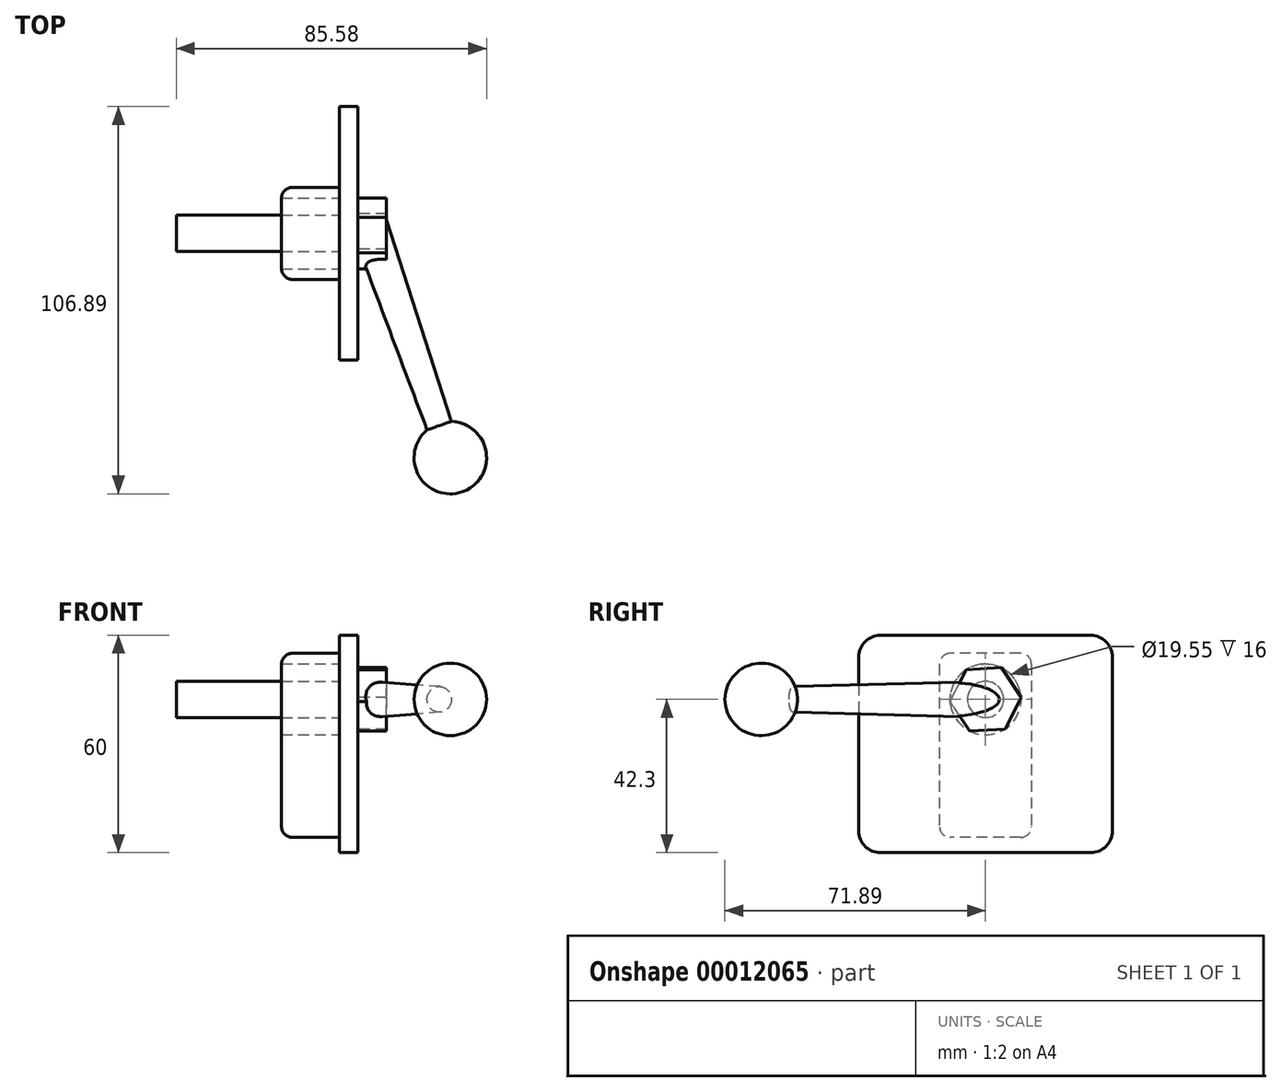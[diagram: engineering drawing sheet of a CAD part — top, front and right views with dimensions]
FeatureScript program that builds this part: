
annotation { "Feature Type Name" : "Feature", "Feature Type Description" : "" }
export const myFeature = defineFeature(function(context is Context, id is Id, definition is map)
    precondition{}
    {
        {
            var Q0;
            Q0=qCreatedBy(makeId("Right.planeOp"),FACE);
            var sketch = newSketch(context, id + "F0", { "sketchPlane" : qUnion([Q0])});
            skCircle(sketch, "E0.cCircle", {"center": v(0, 0) * mm, "radius": 8.5 * mm, "construction": true});
            skLineSegment(sketch, "E0.0", {"start": v(9.8, 0.59) * mm, "end": v(5.4, -8.2) * mm});
            skLineSegment(sketch, "E0.1", {"start": v(5.4, -8.2) * mm, "end": v(-4.39, -8.78) * mm});
            skLineSegment(sketch, "E0.2", {"start": v(-4.39, -8.78) * mm, "end": v(-9.8, -0.59) * mm});
            skLineSegment(sketch, "E0.3", {"start": v(-9.8, -0.59) * mm, "end": v(-5.4, 8.2) * mm});
            skLineSegment(sketch, "E0.4", {"start": v(-5.4, 8.2) * mm, "end": v(4.39, 8.78) * mm});
            skLineSegment(sketch, "E0.5", {"start": v(4.39, 8.78) * mm, "end": v(9.8, 0.59) * mm});
            skPoint(sketch, "E0.0.midPoint", {"position": v(7.6, -3.8) * mm});
            skSolve(sketch);
        }
        {
            var Q0;
            Q0 = qSketchRegion(id + "F0", true);
            extrude(context, id + "F1", {"entities" : qUnion([Q0]), "depth" : 8 * mm});
        }
        {
            var Q0;
            Q0=makeQuery(id+"F1.opExtrude","CAP_FACE",FACE,{"disambiguationData":[OSD([sQuery(id+"F0.wireOp",EDGE,"E0.0"),sQuery(id+"F0.wireOp",EDGE,"E0.1"),sQuery(id+"F0.wireOp",EDGE,"E0.2"),sQuery(id+"F0.wireOp",EDGE,"E0.3"),sQuery(id+"F0.wireOp",EDGE,"E0.4"),sQuery(id+"F0.wireOp",EDGE,"E0.5")])],"isStart":true});
            var sketch = newSketch(context, id + "F2", { "sketchPlane" : qUnion([Q0])});
            skCircle(sketch, "E1", {"center": v(0, 0) * mm, "radius": 5 * mm});
            skSolve(sketch);
        }
        {
            var Q0;
            Q0 = qSketchRegion(id + "F2", true);
            extrude(context, id + "F3", {"entities" : qUnion([Q0]), "operationType" : NewBodyOperationType.ADD, "depth" : 50 * mm});
        }
        {
            var Q0;
            Q0=qCreatedBy(makeId("Right.planeOp"),FACE);
            var sketch = newSketch(context, id + "F4", { "sketchPlane" : qUnion([Q0])});
            skLineSegment(sketch, "E2.bottom", {"start": v(29, 17.7) * mm, "end": v(-29, 17.7) * mm});
            skLineSegment(sketch, "E2.top", {"start": v(29, -42.3) * mm, "end": v(-29, -42.3) * mm});
            skLineSegment(sketch, "E2.left", {"start": v(35, 11.7) * mm, "end": v(35, -36.3) * mm});
            skLineSegment(sketch, "E2.right", {"start": v(-35, 11.7) * mm, "end": v(-35, -36.3) * mm});
            skPoint(sketch, "E3.visualSharp", {"position": v(35, 17.7) * mm});
            skArc(sketch, "E3.filletArc", {"start": v(35, 11.7) * mm, "mid": v(33.24, 15.94) * mm, "end": v(29, 17.7) * mm});
            skPoint(sketch, "E4.visualSharp", {"position": v(-35, 17.7) * mm});
            skArc(sketch, "E4.filletArc", {"start": v(-29, 17.7) * mm, "mid": v(-33.24, 15.94) * mm, "end": v(-35, 11.7) * mm});
            skPoint(sketch, "E5.visualSharp", {"position": v(-35, -42.3) * mm});
            skArc(sketch, "E5.filletArc", {"start": v(-35, -36.3) * mm, "mid": v(-33.24, -40.54) * mm, "end": v(-29, -42.3) * mm});
            skPoint(sketch, "E6.visualSharp", {"position": v(35, -42.3) * mm});
            skArc(sketch, "E6.filletArc", {"start": v(29, -42.3) * mm, "mid": v(33.24, -40.54) * mm, "end": v(35, -36.3) * mm});
            skSolve(sketch);
        }
        {
            var Q0;
            Q0 = qSketchRegion(id + "F4", true);
            extrude(context, id + "F5", {"entities" : qUnion([Q0]), "operationType" : NewBodyOperationType.ADD, "oppositeDirection" : true, "depth" : 5 * mm});
        }
        {
            var Q0;
            Q0=makeQuery(id+"F5.opExtrude","CAP_FACE",FACE,{"disambiguationData":[OSD([sQuery(id+"F4.wireOp",EDGE,"E2.bottom"),sQuery(id+"F4.wireOp",EDGE,"E2.top"),sQuery(id+"F4.wireOp",EDGE,"E2.left"),sQuery(id+"F4.wireOp",EDGE,"E2.right"),sQuery(id+"F4.wireOp",EDGE,"E3.filletArc"),sQuery(id+"F4.wireOp",EDGE,"E4.filletArc"),sQuery(id+"F4.wireOp",EDGE,"E5.filletArc"),sQuery(id+"F4.wireOp",EDGE,"E6.filletArc")])],"isStart":false});
            var sketch = newSketch(context, id + "F6", { "sketchPlane" : qUnion([Q0])});
            skLineSegment(sketch, "E7.bottom", {"start": v(-9.7, 12.7) * mm, "end": v(9.7, 12.7) * mm});
            skLineSegment(sketch, "E7.top", {"start": v(-9.7, -38.1) * mm, "end": v(9.7, -38.1) * mm});
            skLineSegment(sketch, "E7.left", {"start": v(-12.7, 9.7) * mm, "end": v(-12.7, -35.1) * mm});
            skLineSegment(sketch, "E7.right", {"start": v(12.7, 9.7) * mm, "end": v(12.7, -35.1) * mm});
            skCircle(sketch, "E8", {"center": v(0, 0) * mm, "radius": 9.78 * mm});
            skPoint(sketch, "E9.visualSharp", {"position": v(-12.7, 12.7) * mm});
            skArc(sketch, "E9.filletArc", {"start": v(-9.7, 12.7) * mm, "mid": v(-11.82, 11.82) * mm, "end": v(-12.7, 9.7) * mm});
            skPoint(sketch, "E10.visualSharp", {"position": v(12.7, 12.7) * mm});
            skArc(sketch, "E10.filletArc", {"start": v(12.7, 9.7) * mm, "mid": v(11.82, 11.82) * mm, "end": v(9.7, 12.7) * mm});
            skPoint(sketch, "E11.visualSharp", {"position": v(12.7, -38.1) * mm});
            skArc(sketch, "E11.filletArc", {"start": v(9.7, -38.1) * mm, "mid": v(11.82, -37.22) * mm, "end": v(12.7, -35.1) * mm});
            skPoint(sketch, "E12.visualSharp", {"position": v(-12.7, -38.1) * mm});
            skArc(sketch, "E12.filletArc", {"start": v(-12.7, -35.1) * mm, "mid": v(-11.82, -37.22) * mm, "end": v(-9.7, -38.1) * mm});
            skSolve(sketch);
        }
        {
            var Q0;
            Q0 = qSketchRegion(id + "F6", true);
            extrude(context, id + "F7", {"entities" : qUnion([Q0]), "operationType" : NewBodyOperationType.ADD, "depth" : 16 * mm});
        }
        {
            var Q0;
            Q0=makeQuery(id+"F7.opExtrude","CAP_EDGE",EDGE,{"disambiguationData":[OSD([sQuery(id+"F6.wireOp",EDGE,"E7.left")])],"isStart":false});
            fillet(context, id + "F8", {"entities" : qUnion([Q0]), "radius" : 3 * mm, "tangentPropagation" : true, "allowEdgeOverflow" : false});
        }
        {
            var Q0;
            Q0=qCreatedBy(makeId("Top.planeOp"),FACE);
            var sketch = newSketch(context, id + "F9", { "sketchPlane" : qUnion([Q0])});
            skLineSegment(sketch, "E13", {"start": v(7.1, 6.58) * mm, "end": v(4.03, 0) * mm});
            skLineSegment(sketch, "E14", {"start": v(7.1, 6.58) * mm, "end": v(25.85, -51.9) * mm});
            skArc(sketch, "E15", {"start": v(28.87, -71.34) * mm, "mid": v(35.47, -60.36) * mm, "end": v(25.85, -51.9) * mm});
            skLineSegment(sketch, "E16", {"start": v(4.03, 0) * mm, "end": v(28.87, -71.34) * mm});
            skSolve(sketch);
        }
        {
            var Q0;
            Q0=makeQuery(id+"F9.imprint","IMPRINT",FACE,{"disambiguationData":[TD([[makeQuery(id+"F9.imprint","IMPRINT",EDGE,{"derivedFrom":sQuery(id+"F9.wireOp",EDGE,"E13")}),1.0]])]});
            var Q1;
            Q1 = qConstructionFilter(qBodyType(qCreatedBy(id + "F9" ,EDGE), BodyType.WIRE), ConstructionObject.NO);
            var Q2;
            Q2=sQuery(id+"F9.wireOp",EDGE,"E16");
            revolve(context, id + "F10", {"operationType" : NewBodyOperationType.ADD, "entities" : qUnion([Q0]), "surfaceEntities" : qUnion([Q1]), "axis" : qUnion([Q2]), "revolveType" : RevolveType.FULL});
        }
    });
